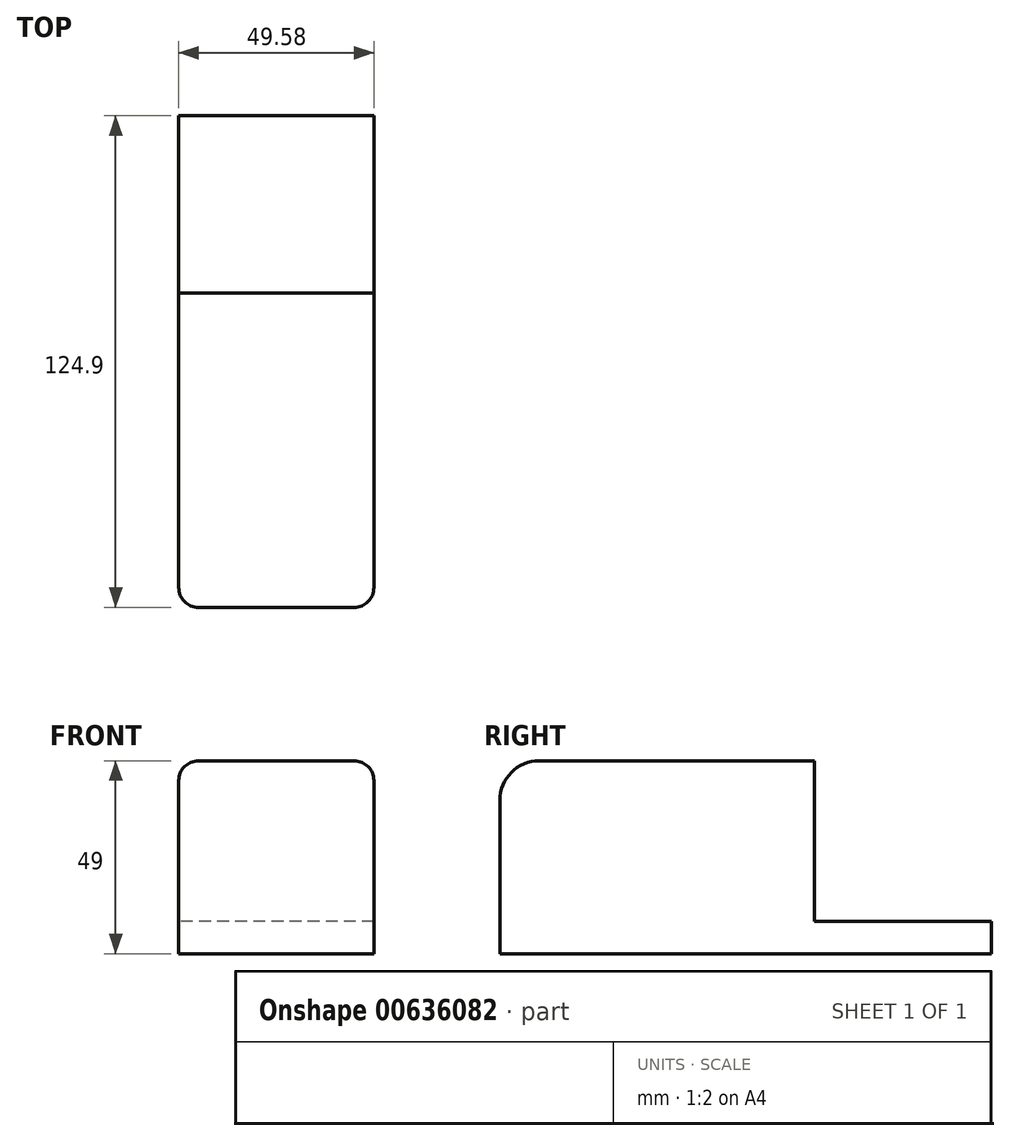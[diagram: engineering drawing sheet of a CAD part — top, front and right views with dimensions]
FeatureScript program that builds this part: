
annotation { "Feature Type Name" : "Feature", "Feature Type Description" : "" }
export const myFeature = defineFeature(function(context is Context, id is Id, definition is map)
    precondition{}
    {
        {
            var Q0;
            Q0=qCreatedBy(makeId("Front.planeOp"),FACE);
            var sketch = newSketch(context, id + "F0", { "sketchPlane" : qUnion([Q0])});
            skLineSegment(sketch, "E0.bottom", {"start": v(24.79, -24.5) * mm, "end": v(-24.79, -24.5) * mm});
            skLineSegment(sketch, "E0.top", {"start": v(24.79, 24.5) * mm, "end": v(-24.79, 24.5) * mm});
            skLineSegment(sketch, "E0.left", {"start": v(24.79, -24.5) * mm, "end": v(24.79, 24.5) * mm});
            skLineSegment(sketch, "E0.right", {"start": v(-24.79, -24.5) * mm, "end": v(-24.79, 24.5) * mm});
            skPoint(sketch, "E0.middle", {"position": v(0, 0) * mm});
            skSolve(sketch);
        }
        {
            var Q0;
            Q0=makeQuery(id+"F0.imprint","IMPRINT",FACE,{"disambiguationData":[TD([[makeQuery(id+"F0.imprint","IMPRINT",EDGE,{"derivedFrom":sQuery(id+"F0.wireOp",EDGE,"E0.bottom")}),-1.0]])]});
            extrude(context, id + "F1", {"entities" : qUnion([Q0]), "oppositeDirection" : true, "depth" : 79.9 * mm, "offsetDistance" : 25 * mm});
        }
        {
            var Q0;
            Q0=makeQuery(id+"F1.opExtrude","CAP_FACE",FACE,{"disambiguationData":[OSD([sQuery(id+"F0.wireOp",EDGE,"E0.bottom"),sQuery(id+"F0.wireOp",EDGE,"E0.top"),sQuery(id+"F0.wireOp",EDGE,"E0.left"),sQuery(id+"F0.wireOp",EDGE,"E0.right")])],"isStart":false});
            var sketch = newSketch(context, id + "F2", { "sketchPlane" : qUnion([Q0])});
            skLineSegment(sketch, "E1.bottom", {"start": v(-24.79, -24.5) * mm, "end": v(24.79, -24.5) * mm});
            skLineSegment(sketch, "E1.top", {"start": v(-24.79, -16.29) * mm, "end": v(24.79, -16.29) * mm});
            skLineSegment(sketch, "E1.left", {"start": v(-24.79, -24.5) * mm, "end": v(-24.79, -16.29) * mm});
            skLineSegment(sketch, "E1.right", {"start": v(24.79, -24.5) * mm, "end": v(24.79, -16.29) * mm});
            skSolve(sketch);
        }
        {
            var Q0;
            Q0=makeQuery(id+"F2.imprint","IMPRINT",FACE,{"disambiguationData":[TD([[makeQuery(id+"F2.imprint","IMPRINT",EDGE,{"derivedFrom":sQuery(id+"F2.wireOp",EDGE,"E1.bottom")}),1.0]])]});
            extrude(context, id + "F3", {"entities" : qUnion([Q0]), "operationType" : NewBodyOperationType.ADD, "depth" : 45 * mm, "offsetDistance" : 25 * mm});
        }
        {
            var Q0;
            Q0=makeQuery(id+"F1.opExtrude","CAP_EDGE",EDGE,{"disambiguationData":[OSD([sQuery(id+"F0.wireOp",EDGE,"E0.top")])],"isStart":true});
            fillet(context, id + "F4", {"entities" : qUnion([Q0]), "radius" : 10 * mm, "tangentPropagation" : true, "allowEdgeOverflow" : false});
        }
        {
            var Q0;
            Q0=makeQuery(id+"F4.opFillet","BLEND_EDGE",EDGE,{"blendedFrom":[makeQuery(id+"F1.opExtrude","CAP_EDGE",EDGE,{"disambiguationData":[OSD([sQuery(id+"F0.wireOp",EDGE,"E0.top")])],"isStart":true}),makeQuery(id+"F3.boolean.opBoolean","MERGE",FACE,{"derivedFrom":[makeQuery(id+"F1.opExtrude","SWEPT_FACE",FACE,{"disambiguationData":[OSD([sQuery(id+"F0.wireOp",EDGE,"E0.left")])]}),makeQuery(id+"F3.opExtrude","SWEPT_FACE",FACE,{"disambiguationData":[OSD([sQuery(id+"F2.wireOp",EDGE,"E1.left")])]})]})],"blendedInto":[makeQuery(id+"F3.boolean.opBoolean","MERGE",FACE,{"derivedFrom":[makeQuery(id+"F1.opExtrude","SWEPT_FACE",FACE,{"disambiguationData":[OSD([sQuery(id+"F0.wireOp",EDGE,"E0.left")])]}),makeQuery(id+"F3.opExtrude","SWEPT_FACE",FACE,{"disambiguationData":[OSD([sQuery(id+"F2.wireOp",EDGE,"E1.left")])]})]})]});
            var Q1;
            Q1=makeQuery(id+"F4.opFillet","BLEND_EDGE",EDGE,{"blendedFrom":[makeQuery(id+"F1.opExtrude","CAP_EDGE",EDGE,{"disambiguationData":[OSD([sQuery(id+"F0.wireOp",EDGE,"E0.top")])],"isStart":true}),makeQuery(id+"F3.boolean.opBoolean","MERGE",FACE,{"derivedFrom":[makeQuery(id+"F1.opExtrude","SWEPT_FACE",FACE,{"disambiguationData":[OSD([sQuery(id+"F0.wireOp",EDGE,"E0.right")])]}),makeQuery(id+"F3.opExtrude","SWEPT_FACE",FACE,{"disambiguationData":[OSD([sQuery(id+"F2.wireOp",EDGE,"E1.right")])]})]})],"blendedInto":[makeQuery(id+"F3.boolean.opBoolean","MERGE",FACE,{"derivedFrom":[makeQuery(id+"F1.opExtrude","SWEPT_FACE",FACE,{"disambiguationData":[OSD([sQuery(id+"F0.wireOp",EDGE,"E0.right")])]}),makeQuery(id+"F3.opExtrude","SWEPT_FACE",FACE,{"disambiguationData":[OSD([sQuery(id+"F2.wireOp",EDGE,"E1.right")])]})]})]});
            fillet(context, id + "F5", {"entities" : qUnion([Q0, Q1]), "radius" : 5 * mm, "tangentPropagation" : true, "allowEdgeOverflow" : false});
        }
    });
